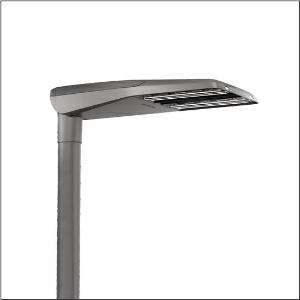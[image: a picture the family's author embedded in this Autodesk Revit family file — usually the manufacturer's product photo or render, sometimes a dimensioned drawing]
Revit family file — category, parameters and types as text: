
# Revit family: streetlight_sl_11_iq_midi___st1_0p1_0_5xc3k51f08me_0ac4
name_source: partatom
category: Lighting Fixtures
units: mm (PartAtom-declared; Revit-internal decimal feet)

## family parameters
Cut with Voids When Loaded = No
Host = Face
Light Source = No
Part Type = Normal
Room Calculation Point = No
Round Connector Dimension = Use Diameter
Shared = No

## types (1)
- --- (1 x LED, 17550 lm, 124.7 W, 3000K)
    Apparent Load = 125 VA
    CIE Flux Codes = 32 65 95 100 100
    Color Rendering = 70
    Color Temperature = 3000K
    Default Elevation = 1800 mm
    Description = Streetlight SL 11 iQ midi, mast luminaire, primary light control with 3 zone facetted reflector, of plastic, silver coated, highly specular, primary optical cover: cover, of PMMA, transparent, light distribution: ST1.0P1.0, light emission: direct distribution, primary light characteristic: asymmetric, installation type: post-top, side-entry, LED, High Power LED, rated luminous flux: 17.550lm, luminous efficacy: 141lm/W, light colour: 730, colour temperature: 3000K, control: Street-Remote, Auto-Match, Temp-Guard, Lumen-Switch, Night-Set, Smart-Wire, Light-Fading, Desk-Remote (wireless, voltage-free reading and setting of iQ features in the workshop via application-optimized NFC function/RFID function), optimised constant luminous flux control (CLO 2.0), with cable H07RN-F 5x 1.5mm², mains connection: 230..240V, AC, 50/60Hz, connection cable pre-assembled, cable length: 12,5m, start of lifetime: 125W, end of service life: 132W, reduction: 57W, luminaire housing, of diecast aluminium, powder-coated, Siteco® metallic grey (DB 702S), please order mast flange separately, inclination adjustable without tools: 0°, 5°, 10°, 15° (post-top) | 0°, -5°, -10°, -15° (side-entry), sealing non-destructively replaceable, multi-level sealing system, length: 780mm, width: 376mm, height: 118mm, mast flange for spigot size: 42mm (side-entry): 5XC10008XM4, 60/48mm (side-entry/post-top): 5XC10108XM2, 76/60mm (side-entry/post-top): 5XC10108XM1, equipment: Power, protection rating (complete): IP66, insulation class (complete): insulation class II (safety insulation), certification: CE, ENEC, VDE, impact resistance: IK09, permissible operating ambient temperature for outdoor applications: -25..+50°C, standard-compliant lighting for roads and squares, Environmental Product Declaration (EPD) tested and certified by an independent institute, packaging unit: 1 piece

Light Distribution: ST1.0P1.0
    Height = 118 mm
    Lamp = 1 x LED
    Lamp Light Flux = 17550 lm
    Lamp Power = 124.7 W
    Lamp count = 1
    Length = 780 mm
    Luminous efficacy = 141 lm/W
    Manufacturer = Siteco
    ModVariant = No
    Model = 5XC3K51F08ME
    Number of Poles = 1
    OnlyDefault = Yes
    Power Factor = 1
    Product Name = Streetlight SL 11 iQ midi | ST1.0P1.0
    Product group = mast luminaire | pylon top
    ProductGroupID = 6100
    Protection Class = Protection class II
    Protection Degree = IP 66
    RLX_Detail_Level = 1
    RLX_Emergency_Light_Flux = 0 lm
    RLX_Emergency_Type = 0
    RLX_Emergency_Type_DB = No
    RlxData = <blob elided: 70737 chars, md5=242b5f45>
    Socket = socket
    Standby Power = 0 W
    System Light Flux = 17550 lm
    System Power = 125 W
    Type Comments = factory setting: luminous flux: 100 % | dim-lin: 254 | 557 mA
    Type Image = l_1005960.jpg
    URL = http://relux.com
    VarID = @adj_021577
    Voltage = 0 V
    Weight = 0.00 kg
    Width = 376 mm

## geometry (parser evidence)
native form markers: Blend x4, Sweep x8
no freeform markers — native parametric forms only
